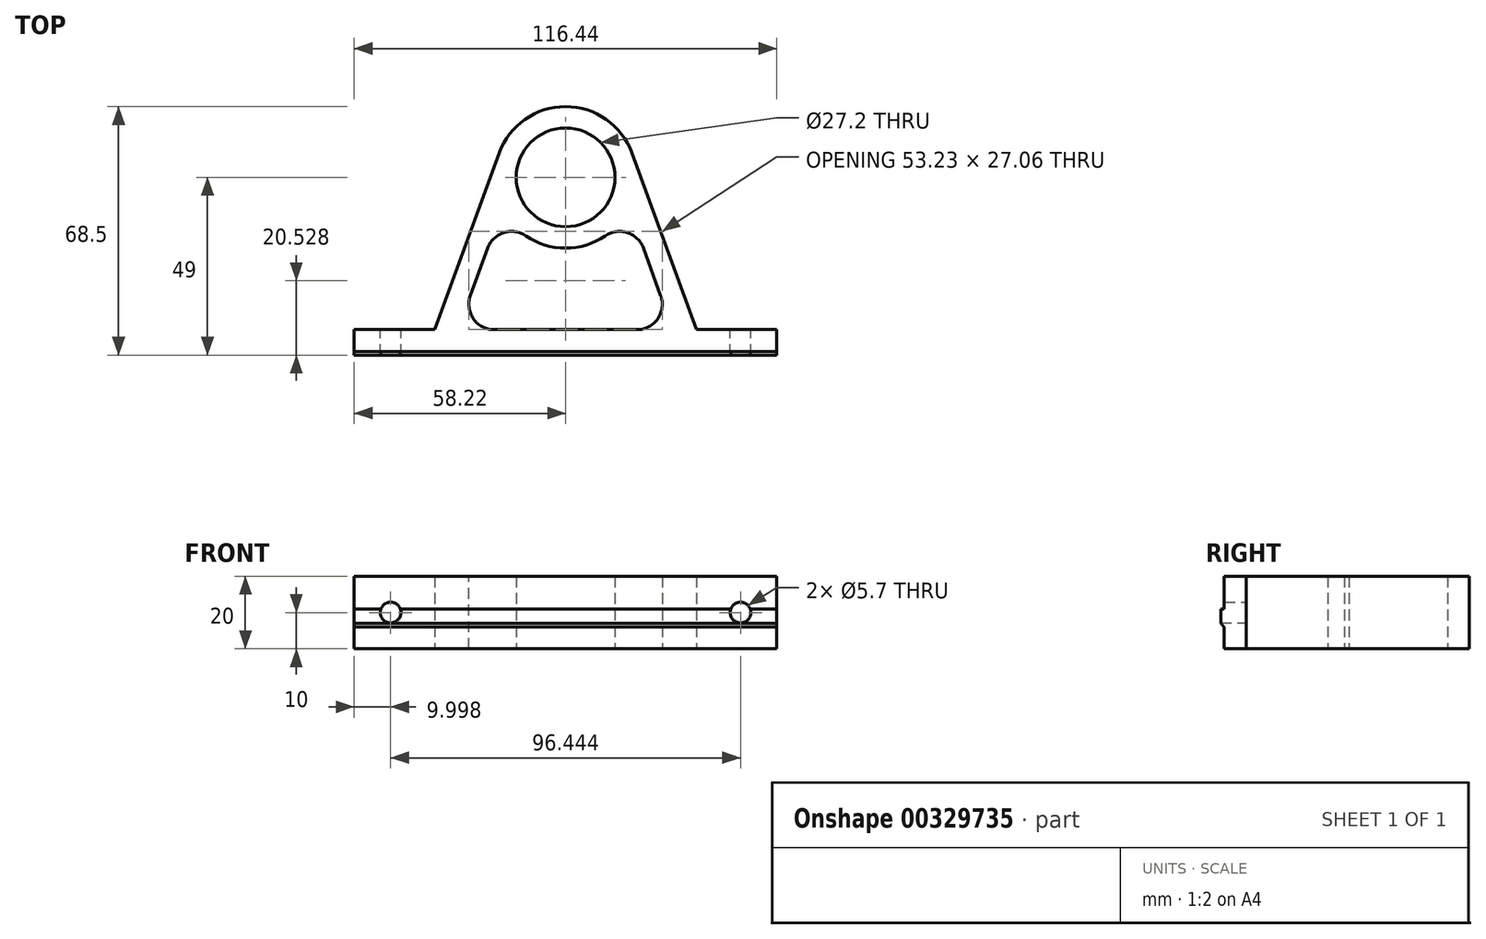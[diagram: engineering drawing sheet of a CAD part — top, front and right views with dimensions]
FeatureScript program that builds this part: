
annotation { "Feature Type Name" : "Feature", "Feature Type Description" : "" }
export const myFeature = defineFeature(function(context is Context, id is Id, definition is map)
    precondition{}
    {
        {
            var Q0;
            Q0=qCreatedBy(makeId("Top.planeOp"),FACE);
            var sketch = newSketch(context, id + "F0", { "sketchPlane" : qUnion([Q0])});
            skCircle(sketch, "E0", {"center": v(0, 48) * mm, "radius": 13.6 * mm});
            skCircle(sketch, "E1", {"center": v(0, 48) * mm, "radius": 19.5 * mm});
            skLineSegment(sketch, "E2", {"start": v(-18.32, 54.67) * mm, "end": v(-38.22, 0) * mm});
            skLineSegment(sketch, "E3", {"start": v(-18.32, 54.67) * mm, "end": v(18.32, 54.67) * mm, "construction": true});
            skLineSegment(sketch, "E4", {"start": v(18.32, 54.67) * mm, "end": v(38.22, 0) * mm});
            skLineSegment(sketch, "E5", {"start": v(-17.5, 39.4) * mm, "end": v(-29.65, 6) * mm});
            skLineSegment(sketch, "E6", {"start": v(17.5, 39.4) * mm, "end": v(29.65, 6) * mm});
            skLineSegment(sketch, "E7", {"start": v(-29.65, 6) * mm, "end": v(29.65, 6) * mm});
            skLineSegment(sketch, "E8", {"start": v(38.22, 0) * mm, "end": v(58.22, 0) * mm});
            skLineSegment(sketch, "E9", {"start": v(-38.22, 0) * mm, "end": v(-58.22, 0) * mm});
            skLineSegment(sketch, "E10.bottom", {"start": v(-58.22, 0) * mm, "end": v(-29.65, 0) * mm});
            skLineSegment(sketch, "E10.top", {"start": v(-58.22, 6) * mm, "end": v(-29.65, 6) * mm});
            skLineSegment(sketch, "E10.left", {"start": v(-58.22, 0) * mm, "end": v(-58.22, 6) * mm});
            skLineSegment(sketch, "E10.right", {"start": v(-29.65, 0) * mm, "end": v(-29.65, 6) * mm});
            skLineSegment(sketch, "E11.bottom", {"start": v(58.22, 0) * mm, "end": v(29.65, 0) * mm});
            skLineSegment(sketch, "E11.top", {"start": v(58.22, 6) * mm, "end": v(29.65, 6) * mm});
            skLineSegment(sketch, "E11.left", {"start": v(58.22, 0) * mm, "end": v(58.22, 6) * mm});
            skLineSegment(sketch, "E11.right", {"start": v(29.65, 0) * mm, "end": v(29.65, 6) * mm});
            skLineSegment(sketch, "E12", {"start": v(-29.65, 0) * mm, "end": v(29.65, 0) * mm});
            skSolve(sketch);
        }
        {
            var Q0;
            Q0=makeQuery(id+"F0.imprint","IMPRINT",FACE,{"disambiguationData":[TD([[makeQuery(id+"F0.imprint","IMPRINT",EDGE,{"derivedFrom":sQuery(id+"F0.wireOp",EDGE,"E0")}),-1.0]])]});
            var Q1;
            {var subQ3=sQuery(id+"F0.wireOp",EDGE,"E5");Q1=makeQuery(id+"F0.imprint","IMPRINT",FACE,{"disambiguationData":[TD([[makeQuery(id+"F0.imprint","IMPRINT",EDGE,{"derivedFrom":subQ3}),-1.0]])]});}
            var Q2;
            {var subQ5=sQuery(id+"F0.wireOp",EDGE,"E10.right");Q2=makeQuery(id+"F0.imprint","IMPRINT",FACE,{"disambiguationData":[TD([[makeQuery(id+"F0.imprint","IMPRINT",EDGE,{"derivedFrom":subQ5}),1.0]])]});}
            var Q3;
            {var subQ5=sQuery(id+"F0.wireOp",EDGE,"E10.left");Q3=makeQuery(id+"F0.imprint","IMPRINT",FACE,{"disambiguationData":[TD([[makeQuery(id+"F0.imprint","IMPRINT",EDGE,{"derivedFrom":subQ5}),-1.0]])]});}
            var Q4;
            Q4=makeQuery(id+"F0.imprint","IMPRINT",FACE,{"disambiguationData":[TD([[makeQuery(id+"F0.imprint","IMPRINT",EDGE,{"derivedFrom":sQuery(id+"F0.wireOp",EDGE,"E7")}),-1.0]])]});
            var Q5;
            {var subQ5=sQuery(id+"F0.wireOp",EDGE,"E11.right");Q5=makeQuery(id+"F0.imprint","IMPRINT",FACE,{"disambiguationData":[TD([[makeQuery(id+"F0.imprint","IMPRINT",EDGE,{"derivedFrom":subQ5}),-1.0]])]});}
            var Q6;
            {var subQ5=sQuery(id+"F0.wireOp",EDGE,"E11.left");Q6=makeQuery(id+"F0.imprint","IMPRINT",FACE,{"disambiguationData":[TD([[makeQuery(id+"F0.imprint","IMPRINT",EDGE,{"derivedFrom":subQ5}),1.0]])]});}
            var Q7;
            {var subQ3=sQuery(id+"F0.wireOp",EDGE,"E6");Q7=makeQuery(id+"F0.imprint","IMPRINT",FACE,{"disambiguationData":[TD([[makeQuery(id+"F0.imprint","IMPRINT",EDGE,{"derivedFrom":subQ3}),1.0]])]});}
            extrude(context, id + "F1", {"entities" : qUnion([Q0, Q1, Q2, Q3, Q4, Q5, Q6, Q7]), "depth" : 20 * mm});
        }
        {
            var Q0;
            Q0=makeQuery(id+"F1.opExtrude","SWEPT_EDGE",EDGE,{"disambiguationData":[OSD([sQuery(id+"F0.wireOp",EDGE,"E1"),sQuery(id+"F0.wireOp",EDGE,"E5")])]});
            var Q1;
            Q1=makeQuery(id+"F1.opExtrude","SWEPT_EDGE",EDGE,{"disambiguationData":[OSD([sQuery(id+"F0.wireOp",EDGE,"E1"),sQuery(id+"F0.wireOp",EDGE,"E6")])]});
            var Q2;
            Q2=makeQuery(id+"F1.opExtrude","SWEPT_EDGE",EDGE,{"disambiguationData":[OSD([sQuery(id+"F0.wireOp",EDGE,"E5"),sQuery(id+"F0.wireOp",EDGE,"E7"),sQuery(id+"F0.wireOp",EDGE,"E10.top"),sQuery(id+"F0.wireOp",EDGE,"E10.right")])]});
            var Q3;
            Q3=makeQuery(id+"F1.opExtrude","SWEPT_EDGE",EDGE,{"disambiguationData":[OSD([sQuery(id+"F0.wireOp",EDGE,"E6"),sQuery(id+"F0.wireOp",EDGE,"E7"),sQuery(id+"F0.wireOp",EDGE,"E11.top"),sQuery(id+"F0.wireOp",EDGE,"E11.right")])]});
            fillet(context, id + "F2", {"entities" : qUnion([Q0, Q1, Q2, Q3]), "radius" : 7 * mm, "tangentPropagation" : true, "allowEdgeOverflow" : false});
        }
        {
            var Q0;
            Q0=makeQuery(id+"F1.opExtrude","SWEPT_FACE",FACE,{"disambiguationData":[OSD([sQuery(id+"F0.wireOp",EDGE,"E10.bottom"),sQuery(id+"F0.wireOp",EDGE,"E11.bottom"),sQuery(id+"F0.wireOp",EDGE,"E12")])]});
            var sketch = newSketch(context, id + "F3", { "sketchPlane" : qUnion([Q0])});
            skLineSegment(sketch, "E13.bottom", {"start": v(-58.22, 11) * mm, "end": v(58.22, 11) * mm});
            skLineSegment(sketch, "E13.top", {"start": v(-58.22, 9) * mm, "end": v(58.22, 9) * mm});
            skLineSegment(sketch, "E13.left", {"start": v(-58.22, 11) * mm, "end": v(-58.22, 9) * mm});
            skLineSegment(sketch, "E13.right", {"start": v(58.22, 11) * mm, "end": v(58.22, 9) * mm});
            skSolve(sketch);
        }
        {
            var Q0;
            Q0=makeQuery(id+"F3.imprint","IMPRINT",FACE,{"disambiguationData":[TD([[makeQuery(id+"F3.imprint","IMPRINT",EDGE,{"derivedFrom":sQuery(id+"F3.wireOp",EDGE,"E13.bottom")}),-1.0]])]});
            extrude(context, id + "F4", {"entities" : qUnion([Q0]), "operationType" : NewBodyOperationType.ADD, "depth" : 1 * mm});
        }
        {
            var Q0;
            Q0=makeQuery(id+"F4.opExtrude","CAP_EDGE",EDGE,{"disambiguationData":[OSD([sQuery(id+"F3.wireOp",EDGE,"E13.bottom")])],"isStart":true});
            var Q1;
            Q1=makeQuery(id+"F4.opExtrude","CAP_EDGE",EDGE,{"disambiguationData":[OSD([sQuery(id+"F3.wireOp",EDGE,"E13.top")])],"isStart":true});
            chamfer(context, id + "F5", {"entities" : qUnion([Q0, Q1]), "width" : 3 * mm, "tangentPropagation" : true});
        }
        {
            var Q0;
            Q0=makeQuery(id+"F1.opExtrude","SWEPT_FACE",FACE,{"disambiguationData":[OSD([sQuery(id+"F0.wireOp",EDGE,"E10.top")])]});
            var sketch = newSketch(context, id + "F6", { "sketchPlane" : qUnion([Q0])});
            skCircle(sketch, "E14", {"center": v(48.22, 10) * mm, "radius": 2.85 * mm});
            skCircle(sketch, "E15", {"center": v(-48.22, 10) * mm, "radius": 2.85 * mm});
            skSolve(sketch);
        }
        {
            var Q0;
            Q0=makeQuery(id+"F6.imprint","IMPRINT",FACE,{"disambiguationData":[TD([[makeQuery(id+"F6.imprint","IMPRINT",EDGE,{"derivedFrom":sQuery(id+"F6.wireOp",EDGE,"E14")}),1.0]])]});
            var Q1;
            Q1=makeQuery(id+"F6.imprint","IMPRINT",FACE,{"disambiguationData":[TD([[makeQuery(id+"F6.imprint","IMPRINT",EDGE,{"derivedFrom":sQuery(id+"F6.wireOp",EDGE,"E15")}),1.0]])]});
            extrude(context, id + "F7", {"entities" : qUnion([Q0, Q1]), "operationType" : NewBodyOperationType.REMOVE, "oppositeDirection" : true, "depth" : 25 * mm});
        }
    });
